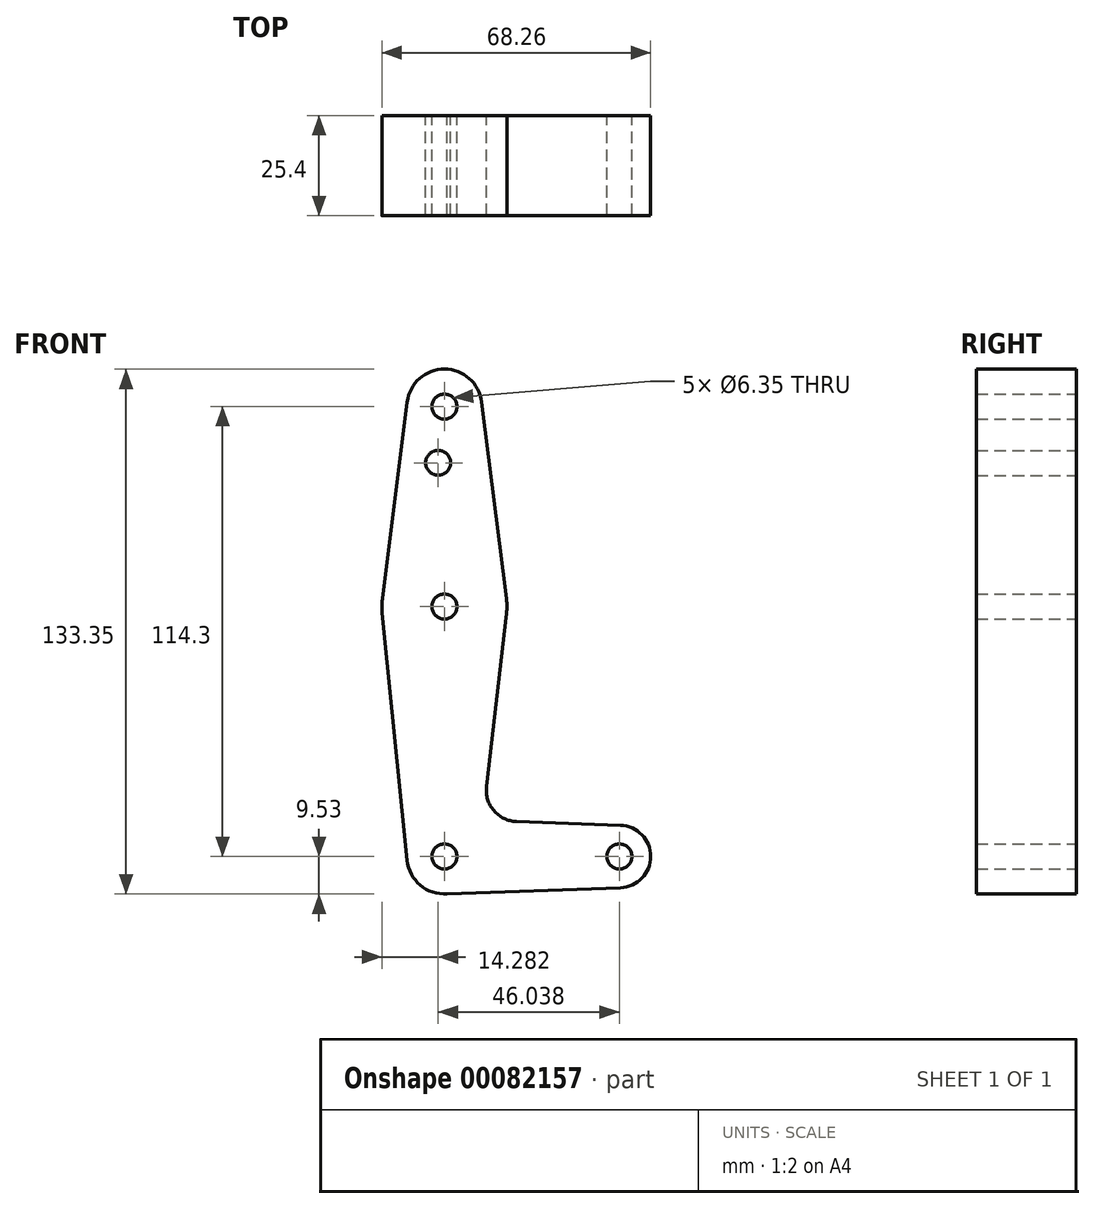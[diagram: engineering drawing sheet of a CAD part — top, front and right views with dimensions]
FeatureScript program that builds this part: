
annotation { "Feature Type Name" : "Feature", "Feature Type Description" : "" }
export const myFeature = defineFeature(function(context is Context, id is Id, definition is map)
    precondition{}
    {
        {
            var Q0;
            Q0=qCreatedBy(makeId("Front.planeOp"),FACE);
            var sketch = newSketch(context, id + "F0", { "sketchPlane" : qUnion([Q0])});
            skCircle(sketch, "E0", {"center": v(0, 0) * mm, "radius": 15.88 * mm});
            skLineSegment(sketch, "E1", {"start": v(0, 50.8) * mm, "end": v(0, 0) * mm, "construction": true});
            skLineSegment(sketch, "E2", {"start": v(0, 0) * mm, "end": v(0, -63.5) * mm, "construction": true});
            skLineSegment(sketch, "E3", {"start": v(0, -63.5) * mm, "end": v(44.45, -63.5) * mm, "construction": true});
            skCircle(sketch, "E4", {"center": v(0, 50.8) * mm, "radius": 9.53 * mm});
            skCircle(sketch, "E5", {"center": v(0, -63.5) * mm, "radius": 9.53 * mm});
            skCircle(sketch, "E6", {"center": v(44.45, -63.5) * mm, "radius": 7.94 * mm});
            skLineSegment(sketch, "E7", {"start": v(0, 50.8) * mm, "end": v(0, -63.5) * mm, "construction": true});
            skLineSegment(sketch, "E8", {"start": v(18.3, -54.63) * mm, "end": v(44.73, -55.57) * mm});
            skArc(sketch, "E9.filletArc", {"start": v(10.69, -45.76) * mm, "mid": v(12.56, -51.86) * mm, "end": v(18.3, -54.63) * mm});
            skLineSegment(sketch, "E10", {"start": v(0, -73.02) * mm, "end": v(44.73, -71.43) * mm});
            skCircle(sketch, "E11", {"center": v(0, 50.8) * mm, "radius": 3.18 * mm});
            skCircle(sketch, "E12", {"center": v(0, 0) * mm, "radius": 3.18 * mm});
            skCircle(sketch, "E13", {"center": v(0, -63.5) * mm, "radius": 3.18 * mm});
            skCircle(sketch, "E14", {"center": v(44.45, -63.5) * mm, "radius": 3.18 * mm});
            skCircle(sketch, "E15", {"center": v(-1.59, 36.53) * mm, "radius": 3.18 * mm});
            skLineSegment(sketch, "E16", {"start": v(-9.45, 52) * mm, "end": v(-15.75, 1.98) * mm});
            skLineSegment(sketch, "E17", {"start": v(9.45, 52) * mm, "end": v(15.75, 1.98) * mm});
            skLineSegment(sketch, "E18", {"start": v(15.77, -1.82) * mm, "end": v(10.69, -45.76) * mm});
            skLineSegment(sketch, "E19", {"start": v(-15.8, -1.59) * mm, "end": v(-9.48, -64.45) * mm});
            skSolve(sketch);
        }
        {
            var Q0;
            Q0 = qSketchRegion(id + "F0", true);
            extrude(context, id + "F1", {"entities" : qUnion([Q0]), "depth" : 25.4 * mm});
        }
    });
